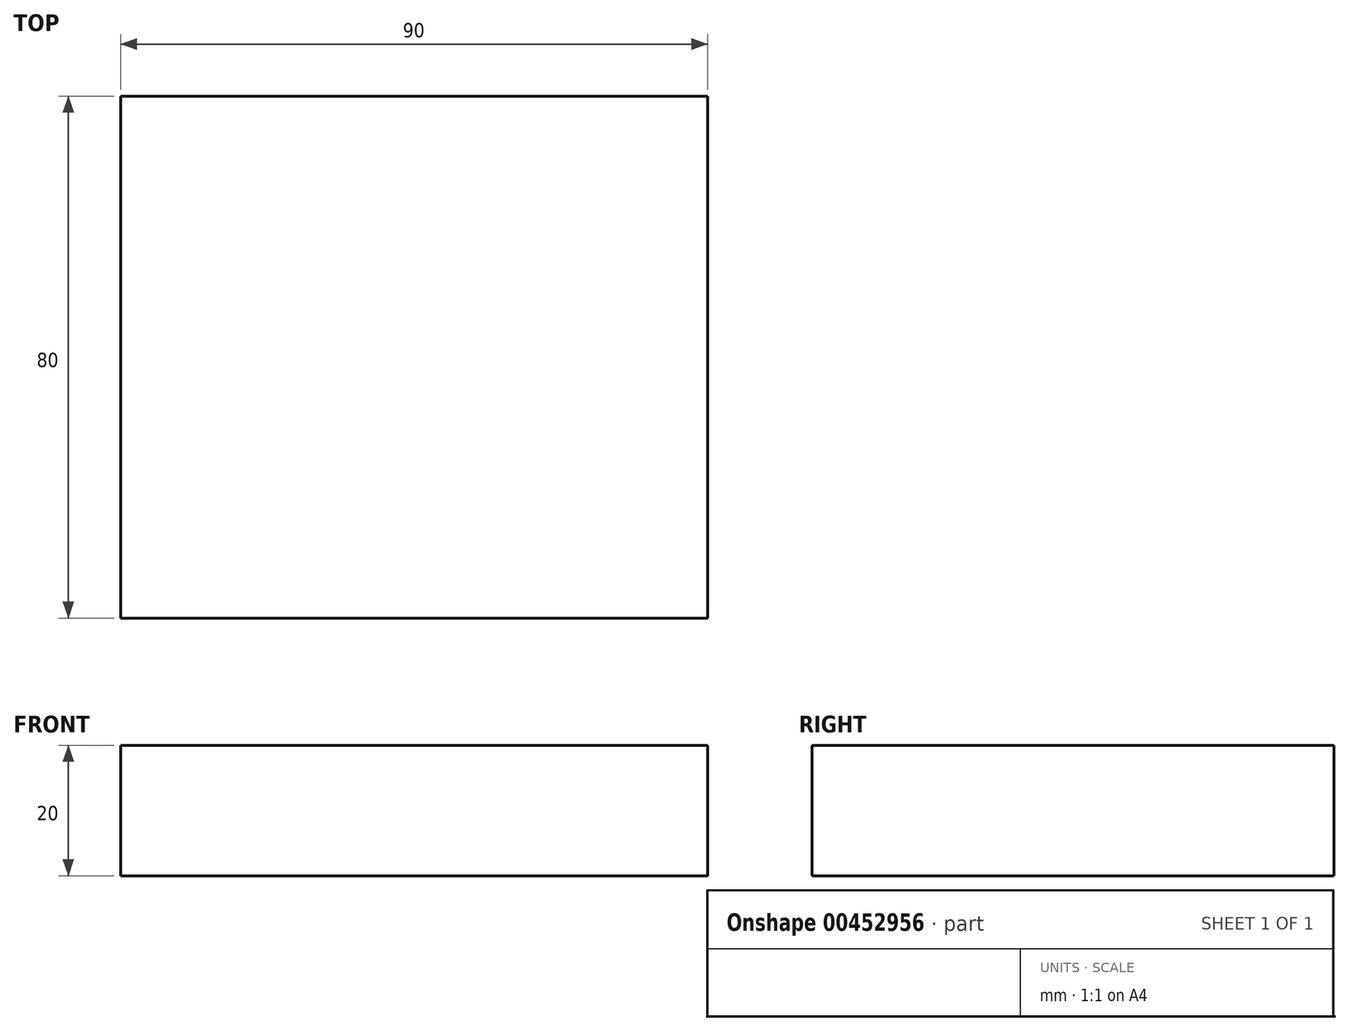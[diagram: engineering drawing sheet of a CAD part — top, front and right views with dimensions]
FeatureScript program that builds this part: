
annotation { "Feature Type Name" : "Feature", "Feature Type Description" : "" }
export const myFeature = defineFeature(function(context is Context, id is Id, definition is map)
    precondition{}
    {
        {
            var Q0;
            Q0=qCreatedBy(makeId("Top.planeOp"),FACE);
            var sketch = newSketch(context, id + "F0", { "sketchPlane" : qUnion([Q0])});
            skLineSegment(sketch, "E0.bottom", {"start": v(-45, 40) * mm, "end": v(45, 40) * mm});
            skLineSegment(sketch, "E0.top", {"start": v(-45, -40) * mm, "end": v(45, -40) * mm});
            skLineSegment(sketch, "E0.left", {"start": v(-45, 40) * mm, "end": v(-45, -40) * mm});
            skLineSegment(sketch, "E0.right", {"start": v(45, 40) * mm, "end": v(45, -40) * mm});
            skLineSegment(sketch, "E1", {"start": v(-45, 0) * mm, "end": v(45, 0) * mm});
            skSolve(sketch);
        }
        {
            var Q0;
            Q0 = qSketchRegion(id + "F0", true);
            extrude(context, id + "F1", {"entities" : qUnion([Q0]), "depth" : 20 * mm, "offsetDistance" : 25 * mm});
        }
    });
